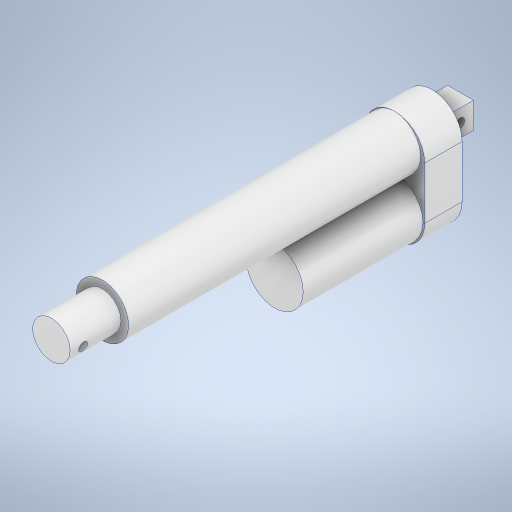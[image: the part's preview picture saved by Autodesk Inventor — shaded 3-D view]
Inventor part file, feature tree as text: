
AUTODESK INVENTOR PART (.ipt)
format: ipt  version: 2024 (Build 280153000, 153)  size: 309,760 bytes
history: native  units: mm
features: extrude x6, sketch x6, other x1
ambient origin geometry x8: Origin, YZ Plane, XZ Plane, XY Plane, X Axis, Y Axis, Z Axis, Center Point
bodies: Body1 (feature_tree)
feature tree (13):
  other  "솔리드1"
  extrude  "돌출1"  Depth=34.8mm
  extrude  "돌출2"  Depth=40.0mm
  extrude  "돌출3"  Depth=25.0mm TaperAngle=0.0deg
  extrude  "돌출4"  Depth=35.0mm
  extrude  "돌출5"  Depth=195.0mm TaperAngle=0.0deg
  extrude  "돌출6"  Depth=25.0mm
  sketch  "스케치1"
  sketch  "스케치2"
  sketch  "스케치3"
  sketch  "스케치5"
  sketch  "스케치6"
  sketch  "스케치7"
